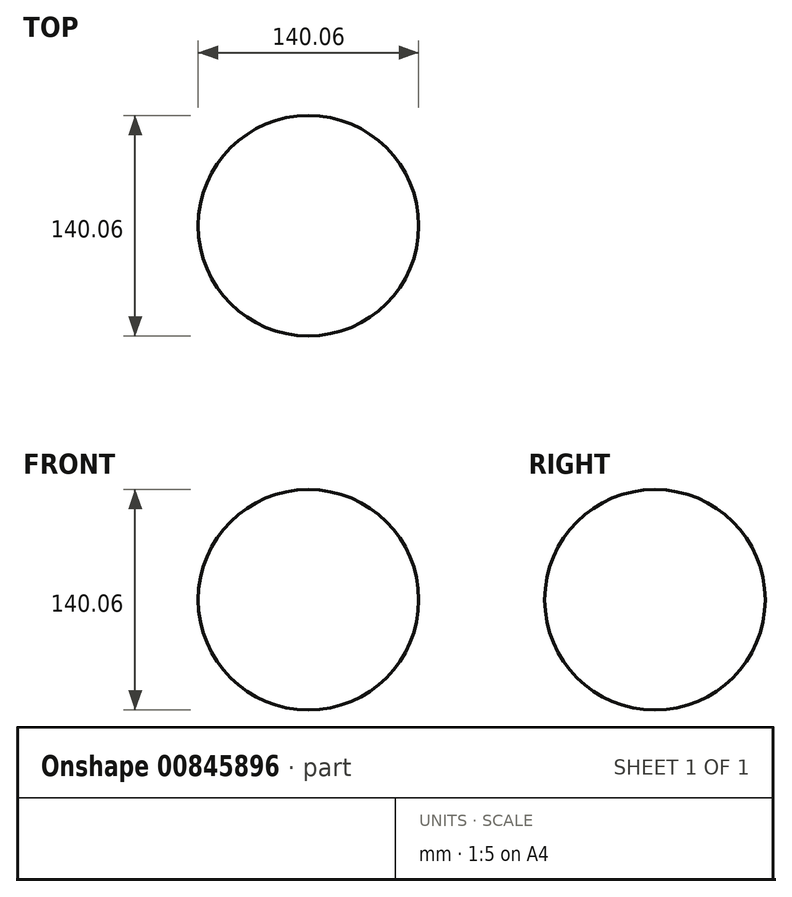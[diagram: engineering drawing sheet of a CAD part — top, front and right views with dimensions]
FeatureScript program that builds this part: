
annotation { "Feature Type Name" : "Feature", "Feature Type Description" : "" }
export const myFeature = defineFeature(function(context is Context, id is Id, definition is map)
    precondition{}
    {
        {
            var Q0;
            Q0=qCreatedBy(makeId("Front.planeOp"),FACE);
            var sketch = newSketch(context, id + "F0", { "sketchPlane" : qUnion([Q0])});
            skCircle(sketch, "E0", {"center": v(0, 0) * mm, "radius": 70.03 * mm});
            skLineSegment(sketch, "E1", {"start": v(0, 76.35) * mm, "end": v(0, -76.17) * mm});
            skSolve(sketch);
        }
        {
            var Q0;
            {var subQ0=sQuery(id+"F0.wireOp",EDGE,"E1");var subQ1=sQuery(id+"F0.wireOp",EDGE,"E0");var subQ2=makeQuery(id+"F0.imprint","INTERSECT",VERTEX,{"disambiguationData":[OD(0.0)],"derivedFrom":[subQ1,subQ0]});Q0=makeQuery(id+"F0.imprint","IMPRINT",FACE,{"disambiguationData":[TD([[makeQuery(id+"F0.imprint","IMPRINT",EDGE,{"disambiguationData":[TD([[subQ2,-1.0]])],"derivedFrom":subQ1}),1.0]])]});}
            var Q1;
            Q1=sQuery(id+"F0.wireOp",EDGE,"E1");
            revolve(context, id + "F1", {"surfaceOperationType" : NewSurfaceOperationType.NEW, "entities" : qUnion([Q0]), "axis" : qUnion([Q1]), "revolveType" : RevolveType.FULL});
        }
    });
